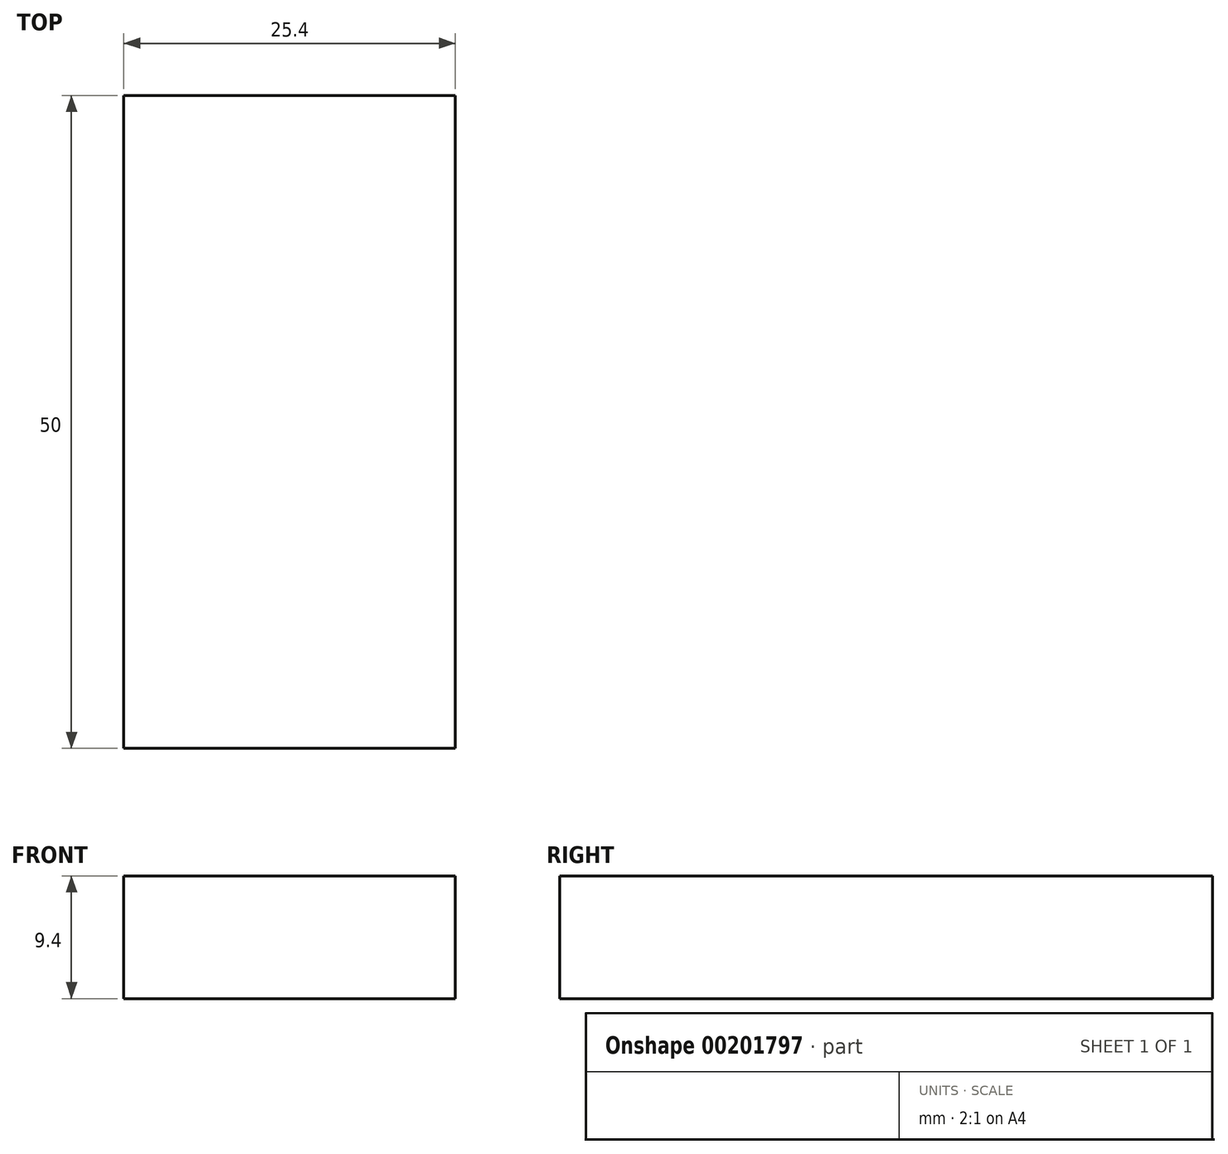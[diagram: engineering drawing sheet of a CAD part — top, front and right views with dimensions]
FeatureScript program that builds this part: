
annotation { "Feature Type Name" : "Feature", "Feature Type Description" : "" }
export const myFeature = defineFeature(function(context is Context, id is Id, definition is map)
    precondition{}
    {
        {
            var Q0;
            Q0=qCreatedBy(makeId("Top.planeOp"),FACE);
            var sketch = newSketch(context, id + "F0", { "sketchPlane" : qUnion([Q0])});
            skLineSegment(sketch, "E0", {"start": v(0, 98.44) * mm, "end": v(0, -111.97) * mm, "construction": true});
            skLineSegment(sketch, "E1", {"start": v(-103.45, 0) * mm, "end": v(119.48, 0) * mm, "construction": true});
            skLineSegment(sketch, "E2.bottom", {"start": v(-12.7, 25) * mm, "end": v(12.7, 25) * mm});
            skLineSegment(sketch, "E2.top", {"start": v(-12.7, -25) * mm, "end": v(12.7, -25) * mm});
            skLineSegment(sketch, "E2.left", {"start": v(-12.7, 25) * mm, "end": v(-12.7, -25) * mm});
            skLineSegment(sketch, "E2.right", {"start": v(12.7, 25) * mm, "end": v(12.7, -25) * mm});
            skPoint(sketch, "E3", {"position": v(0, 25) * mm});
            skPoint(sketch, "E4", {"position": v(12.7, 0) * mm});
            skSolve(sketch);
        }
        {
            var Q0;
            Q0 = qSketchRegion(id + "F0", true);
            extrude(context, id + "F1", {"entities" : qUnion([Q0]), "oppositeDirection" : true, "depth" : (.37 * 25.4) * mm});
        }
    });
